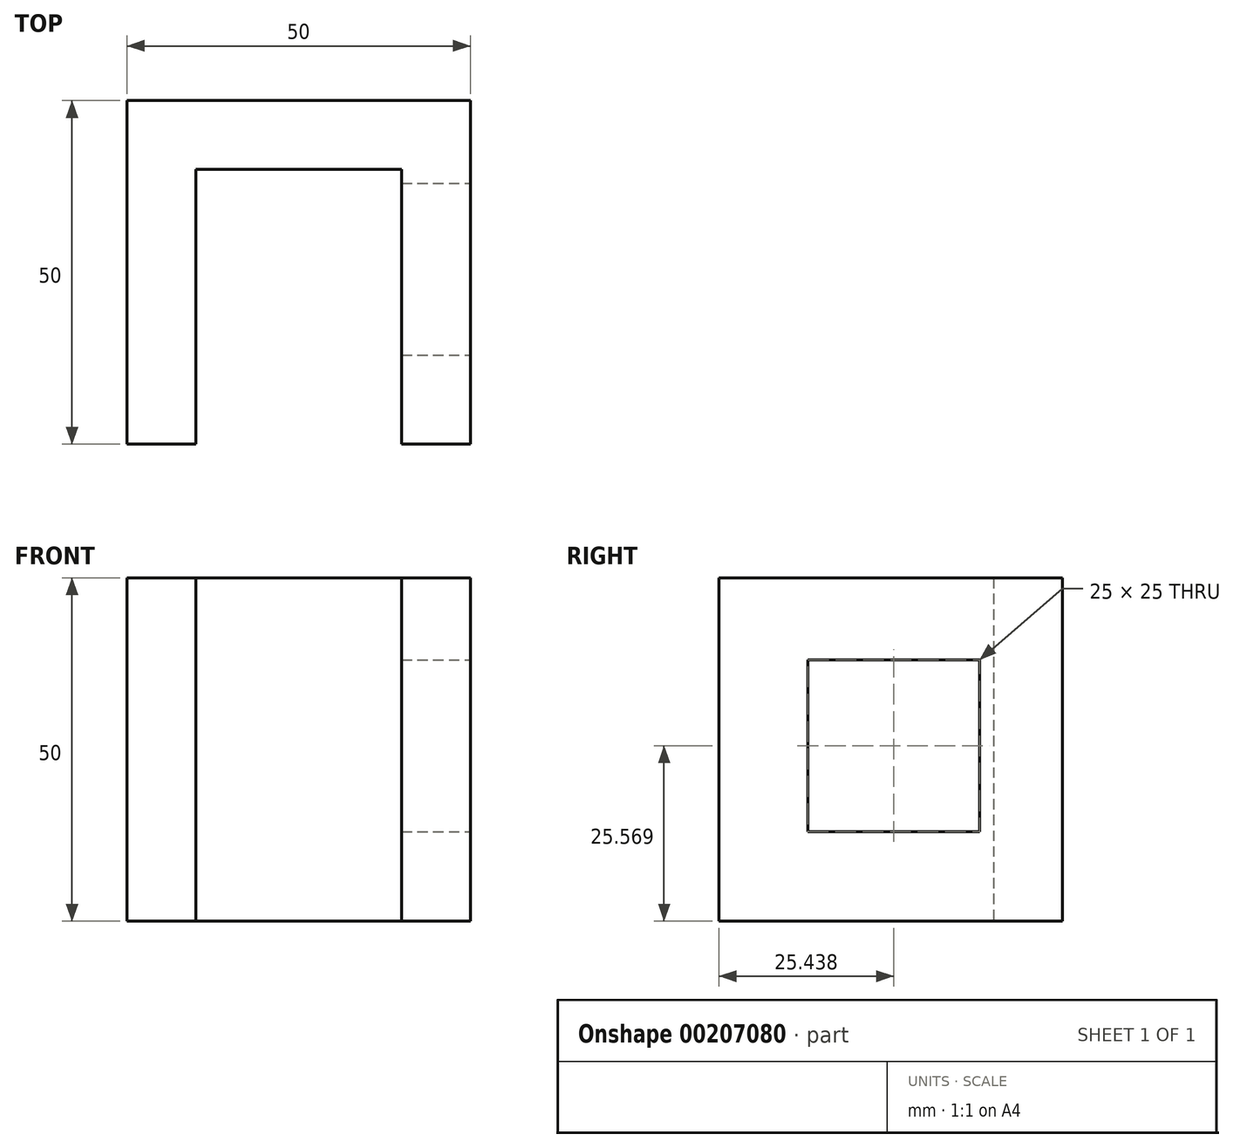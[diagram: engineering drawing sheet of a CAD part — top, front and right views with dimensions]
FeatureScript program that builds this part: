
annotation { "Feature Type Name" : "Feature", "Feature Type Description" : "" }
export const myFeature = defineFeature(function(context is Context, id is Id, definition is map)
    precondition{}
    {
        {
            var Q0;
            Q0=qCreatedBy(makeId("Top.planeOp"),FACE);
            var sketch = newSketch(context, id + "F0", { "sketchPlane" : qUnion([Q0])});
            skLineSegment(sketch, "E0.bottom", {"start": v(0, 0) * mm, "end": v(10, 0) * mm});
            skLineSegment(sketch, "E0.top", {"start": v(0, 50) * mm, "end": v(50, 50) * mm});
            skLineSegment(sketch, "E0.left", {"start": v(0, 0) * mm, "end": v(0, 50) * mm});
            skLineSegment(sketch, "E0.right", {"start": v(50, 0) * mm, "end": v(50, 50) * mm});
            skLineSegment(sketch, "E1.0", {"start": v(40, 0) * mm, "end": v(40, 40) * mm});
            skLineSegment(sketch, "E1.1", {"start": v(10, 40) * mm, "end": v(40, 40) * mm});
            skLineSegment(sketch, "E1.2", {"start": v(10, 0) * mm, "end": v(10, 40) * mm});
            skLineSegment(sketch, "E2.trimOffspring", {"start": v(40, 0) * mm, "end": v(50, 0) * mm});
            skSolve(sketch);
        }
        {
            var Q0;
            Q0=makeQuery(id+"F0.imprint","IMPRINT",FACE,{"disambiguationData":[TD([[makeQuery(id+"F0.imprint","IMPRINT",EDGE,{"derivedFrom":sQuery(id+"F0.wireOp",EDGE,"E0.bottom")}),1.0]])]});
            extrude(context, id + "F1", {"entities" : qUnion([Q0]), "depth" : 50 * mm});
        }
        {
            var Q0;
            Q0=makeQuery(id+"F1.opExtrude","SWEPT_FACE",FACE,{"disambiguationData":[OSD([sQuery(id+"F0.wireOp",EDGE,"E0.right")])]});
            var sketch = newSketch(context, id + "F2", { "sketchPlane" : qUnion([Q0])});
            skLineSegment(sketch, "E3.bottom", {"start": v(12.94, 38.07) * mm, "end": v(37.94, 38.07) * mm});
            skLineSegment(sketch, "E3.top", {"start": v(12.94, 13.07) * mm, "end": v(37.94, 13.07) * mm});
            skLineSegment(sketch, "E3.left", {"start": v(12.94, 38.07) * mm, "end": v(12.94, 13.07) * mm});
            skLineSegment(sketch, "E3.right", {"start": v(37.94, 38.07) * mm, "end": v(37.94, 13.07) * mm});
            skSolve(sketch);
        }
        {
            var Q0;
            Q0=makeQuery(id+"F2.imprint","IMPRINT",FACE,{"disambiguationData":[TD([[makeQuery(id+"F2.imprint","IMPRINT",EDGE,{"derivedFrom":sQuery(id+"F2.wireOp",EDGE,"E3.bottom")}),-1.0]])]});
            extrude(context, id + "F3", {"entities" : qUnion([Q0]), "operationType" : NewBodyOperationType.REMOVE, "oppositeDirection" : true, "depth" : 27 * mm});
        }
    });
